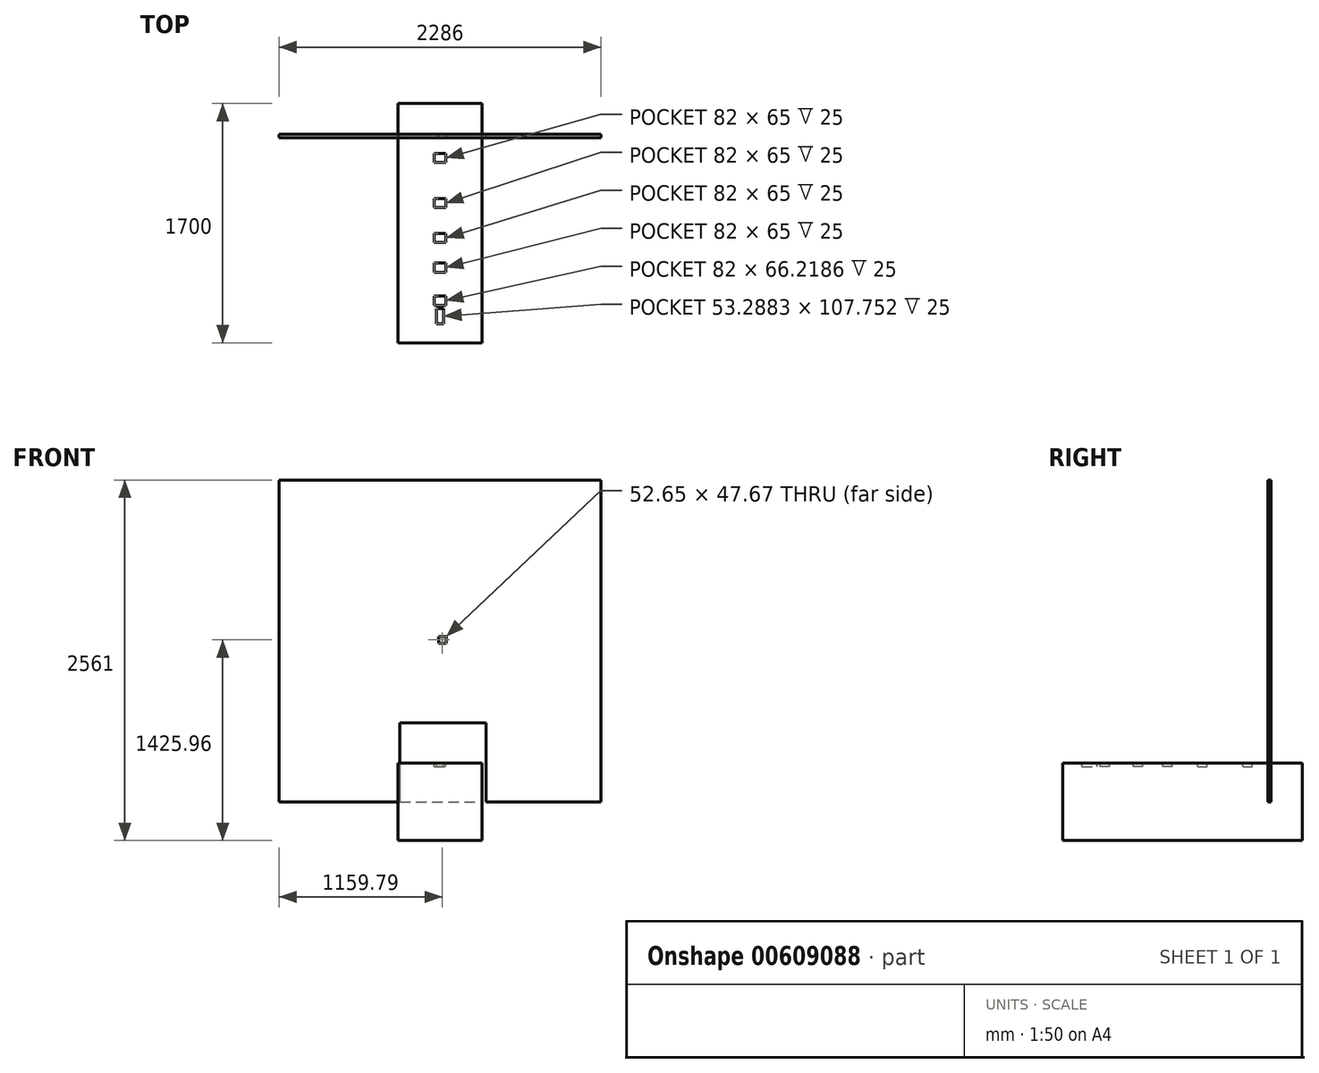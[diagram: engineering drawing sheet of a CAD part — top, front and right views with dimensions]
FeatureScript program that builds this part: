
annotation { "Feature Type Name" : "Feature", "Feature Type Description" : "" }
export const myFeature = defineFeature(function(context is Context, id is Id, definition is map)
    precondition{}
    {
        {
            var Q0;
            Q0=qCreatedBy(makeId("Front.planeOp"),FACE);
            var sketch = newSketch(context, id + "F0", { "sketchPlane" : qUnion([Q0])});
            skLineSegment(sketch, "E0.bottom", {"start": v(-300, 275) * mm, "end": v(300, 275) * mm});
            skLineSegment(sketch, "E0.top", {"start": v(-300, -275) * mm, "end": v(300, -275) * mm});
            skLineSegment(sketch, "E0.left", {"start": v(-300, 275) * mm, "end": v(-300, -275) * mm});
            skLineSegment(sketch, "E0.right", {"start": v(300, 275) * mm, "end": v(300, -275) * mm});
            skPoint(sketch, "E0.middle", {"position": v(0, 0) * mm});
            skSolve(sketch);
        }
        {
            var Q0;
            Q0=makeQuery(id+"F0.imprint","IMPRINT",FACE,{"disambiguationData":[TD([[makeQuery(id+"F0.imprint","IMPRINT",EDGE,{"derivedFrom":sQuery(id+"F0.wireOp",EDGE,"E0.bottom")}),-1.0]])]});
            extrude(context, id + "F1", {"entities" : qUnion([Q0]), "depth" : 1700 * mm, "offsetDistance" : 25 * mm});
        }
        {
            var Q0;
            Q0=makeQuery(id+"F1.opExtrude","SWEPT_FACE",FACE,{"disambiguationData":[OSD([sQuery(id+"F0.wireOp",EDGE,"E0.bottom")])]});
            var sketch = newSketch(context, id + "F2", { "sketchPlane" : qUnion([Q0])});
            skLineSegment(sketch, "E1.bottom", {"start": v(-40.51, -419.34) * mm, "end": v(41.49, -419.34) * mm});
            skLineSegment(sketch, "E1.top", {"start": v(-40.51, -354.34) * mm, "end": v(41.49, -354.34) * mm});
            skLineSegment(sketch, "E1.left", {"start": v(-40.51, -419.34) * mm, "end": v(-40.51, -354.34) * mm});
            skLineSegment(sketch, "E1.right", {"start": v(41.49, -419.34) * mm, "end": v(41.49, -354.34) * mm});
            skLineSegment(sketch, "E2.bottom", {"start": v(-41.91, -740.5) * mm, "end": v(40.09, -740.5) * mm});
            skLineSegment(sketch, "E2.top", {"start": v(-41.91, -675.5) * mm, "end": v(40.09, -675.5) * mm});
            skLineSegment(sketch, "E2.left", {"start": v(-41.91, -740.5) * mm, "end": v(-41.91, -675.5) * mm});
            skLineSegment(sketch, "E2.right", {"start": v(40.09, -740.5) * mm, "end": v(40.09, -675.5) * mm});
            skLineSegment(sketch, "E3.bottom", {"start": v(-40.8, -922.94) * mm, "end": v(41.2, -922.94) * mm});
            skLineSegment(sketch, "E3.top", {"start": v(-40.8, -987.94) * mm, "end": v(41.2, -987.94) * mm});
            skLineSegment(sketch, "E3.left", {"start": v(-40.8, -922.94) * mm, "end": v(-40.8, -987.94) * mm});
            skLineSegment(sketch, "E3.right", {"start": v(41.2, -922.94) * mm, "end": v(41.2, -987.94) * mm});
            skLineSegment(sketch, "E4.bottom", {"start": v(-41.6, -1133.38) * mm, "end": v(40.4, -1133.38) * mm});
            skLineSegment(sketch, "E4.top", {"start": v(-41.6, -1198.38) * mm, "end": v(40.4, -1198.38) * mm});
            skLineSegment(sketch, "E4.left", {"start": v(-41.6, -1133.38) * mm, "end": v(-41.6, -1198.38) * mm});
            skLineSegment(sketch, "E4.right", {"start": v(40.4, -1133.38) * mm, "end": v(40.4, -1198.38) * mm});
            skLineSegment(sketch, "E5.bottom", {"start": v(-42.15, -1367.52) * mm, "end": v(39.85, -1367.52) * mm});
            skLineSegment(sketch, "E5.top", {"start": v(-42.15, -1433.74) * mm, "end": v(39.85, -1433.74) * mm});
            skLineSegment(sketch, "E5.left", {"start": v(-42.15, -1367.52) * mm, "end": v(-42.15, -1433.74) * mm});
            skLineSegment(sketch, "E5.right", {"start": v(39.85, -1367.52) * mm, "end": v(39.85, -1433.74) * mm});
            skLineSegment(sketch, "E6.bottom", {"start": v(26.44, -1564.35) * mm, "end": v(-26.85, -1564.35) * mm});
            skLineSegment(sketch, "E6.top", {"start": v(26.44, -1456.6) * mm, "end": v(-26.85, -1456.6) * mm});
            skLineSegment(sketch, "E6.left", {"start": v(26.44, -1564.35) * mm, "end": v(26.44, -1456.6) * mm});
            skLineSegment(sketch, "E6.right", {"start": v(-26.85, -1564.35) * mm, "end": v(-26.85, -1456.6) * mm});
            skSolve(sketch);
        }
        {
            var Q0;
            Q0=makeQuery(id+"F2.imprint","IMPRINT",FACE,{"disambiguationData":[TD([[makeQuery(id+"F2.imprint","IMPRINT",EDGE,{"derivedFrom":sQuery(id+"F2.wireOp",EDGE,"E6.bottom")}),-1.0]])]});
            var Q1;
            Q1=makeQuery(id+"F2.imprint","IMPRINT",FACE,{"disambiguationData":[TD([[makeQuery(id+"F2.imprint","IMPRINT",EDGE,{"derivedFrom":sQuery(id+"F2.wireOp",EDGE,"E5.bottom")}),-1.0]])]});
            var Q2;
            Q2=makeQuery(id+"F2.imprint","IMPRINT",FACE,{"disambiguationData":[TD([[makeQuery(id+"F2.imprint","IMPRINT",EDGE,{"derivedFrom":sQuery(id+"F2.wireOp",EDGE,"E4.bottom")}),-1.0]])]});
            var Q3;
            Q3=makeQuery(id+"F2.imprint","IMPRINT",FACE,{"disambiguationData":[TD([[makeQuery(id+"F2.imprint","IMPRINT",EDGE,{"derivedFrom":sQuery(id+"F2.wireOp",EDGE,"E3.bottom")}),-1.0]])]});
            var Q4;
            Q4=makeQuery(id+"F2.imprint","IMPRINT",FACE,{"disambiguationData":[TD([[makeQuery(id+"F2.imprint","IMPRINT",EDGE,{"derivedFrom":sQuery(id+"F2.wireOp",EDGE,"E2.bottom")}),1.0]])]});
            var Q5;
            Q5=makeQuery(id+"F2.imprint","IMPRINT",FACE,{"disambiguationData":[TD([[makeQuery(id+"F2.imprint","IMPRINT",EDGE,{"derivedFrom":sQuery(id+"F2.wireOp",EDGE,"E1.bottom")}),1.0]])]});
            extrude(context, id + "F3", {"entities" : qUnion([Q0, Q1, Q2, Q3, Q4, Q5]), "operationType" : NewBodyOperationType.REMOVE, "oppositeDirection" : true, "depth" : 25 * mm, "offsetDistance" : 25 * mm});
        }
        {
            var Q0;
            Q0=qCreatedBy(makeId("Top.planeOp"),FACE);
            var sketch = newSketch(context, id + "F4", { "sketchPlane" : qUnion([Q0])});
            skLineSegment(sketch, "E7.bottom", {"start": v(-1143, -219.2) * mm, "end": v(1143, -219.2) * mm});
            skLineSegment(sketch, "E7.top", {"start": v(-1143, -244.6) * mm, "end": v(1143, -244.6) * mm});
            skLineSegment(sketch, "E7.left", {"start": v(-1143, -219.2) * mm, "end": v(-1143, -244.6) * mm});
            skLineSegment(sketch, "E7.right", {"start": v(1143, -219.2) * mm, "end": v(1143, -244.6) * mm});
            skPoint(sketch, "E7.middle", {"position": v(0, -231.9) * mm});
            skSolve(sketch);
        }
        {
            var Q0;
            Q0=makeQuery(id+"F4.imprint","IMPRINT",FACE,{"disambiguationData":[TD([[makeQuery(id+"F4.imprint","IMPRINT",EDGE,{"derivedFrom":sQuery(id+"F4.wireOp",EDGE,"E7.bottom")}),-1.0]])]});
            extrude(context, id + "F5", {"entities" : qUnion([Q0]), "depth" : 2286 * mm, "offsetDistance" : 25 * mm});
        }
        {
            var Q0;
            Q0=makeQuery(id+"F5.opExtrude","SWEPT_FACE",FACE,{"disambiguationData":[OSD([sQuery(id+"F4.wireOp",EDGE,"E7.bottom")])]});
            var sketch = newSketch(context, id + "F6", { "sketchPlane" : qUnion([Q0])});
            skLineSegment(sketch, "E8.bottom", {"start": v(-43.11, 1174.8) * mm, "end": v(9.53, 1174.8) * mm});
            skLineSegment(sketch, "E8.top", {"start": v(-43.11, 1127.13) * mm, "end": v(9.53, 1127.13) * mm});
            skLineSegment(sketch, "E8.left", {"start": v(-43.11, 1174.8) * mm, "end": v(-43.11, 1127.13) * mm});
            skLineSegment(sketch, "E8.right", {"start": v(9.53, 1174.8) * mm, "end": v(9.53, 1127.13) * mm});
            skSolve(sketch);
        }
        {
            var Q0;
            Q0=makeQuery(id+"F6.imprint","IMPRINT",FACE,{"disambiguationData":[TD([[makeQuery(id+"F6.imprint","IMPRINT",EDGE,{"derivedFrom":sQuery(id+"F6.wireOp",EDGE,"E8.bottom")}),-1.0]])]});
            extrude(context, id + "F7", {"entities" : qUnion([Q0]), "operationType" : NewBodyOperationType.REMOVE, "oppositeDirection" : true, "depth" : 50.8 * mm, "offsetDistance" : 25 * mm});
        }
        {
            var Q0;
            Q0=makeQuery(id+"F5.opExtrude","CAP_FACE",FACE,{"disambiguationData":[OSD([sQuery(id+"F4.wireOp",EDGE,"E7.bottom"),sQuery(id+"F4.wireOp",EDGE,"E7.top"),sQuery(id+"F4.wireOp",EDGE,"E7.left"),sQuery(id+"F4.wireOp",EDGE,"E7.right")])],"isStart":true});
            var sketch = newSketch(context, id + "F8", { "sketchPlane" : qUnion([Q0])});
            skLineSegment(sketch, "E9.bottom", {"start": v(-286.15, 244.6) * mm, "end": v(325.94, 244.6) * mm});
            skLineSegment(sketch, "E9.top", {"start": v(-286.15, 219.2) * mm, "end": v(325.94, 219.2) * mm});
            skLineSegment(sketch, "E9.left", {"start": v(-286.15, 244.6) * mm, "end": v(-286.15, 219.2) * mm});
            skLineSegment(sketch, "E9.right", {"start": v(325.94, 244.6) * mm, "end": v(325.94, 219.2) * mm});
            skSolve(sketch);
        }
        {
            var Q0;
            Q0=makeQuery(id+"F8.imprint","IMPRINT",FACE,{"disambiguationData":[TD([[makeQuery(id+"F8.imprint","IMPRINT",EDGE,{"derivedFrom":sQuery(id+"F8.wireOp",EDGE,"E9.bottom")}),-1.0]])]});
            extrude(context, id + "F9", {"entities" : qUnion([Q0]), "operationType" : NewBodyOperationType.REMOVE, "oppositeDirection" : true, "depth" : 560 * mm, "offsetDistance" : 25 * mm});
        }
    });
